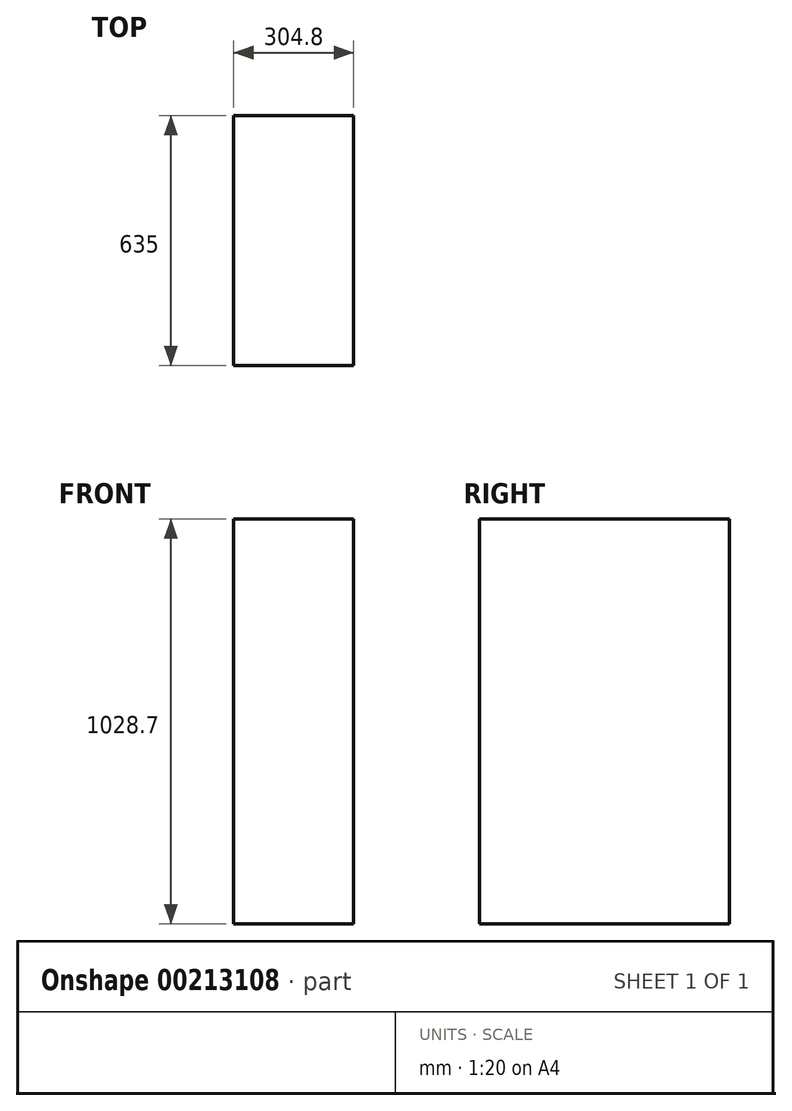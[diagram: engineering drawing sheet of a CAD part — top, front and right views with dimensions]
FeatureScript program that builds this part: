
annotation { "Feature Type Name" : "Feature", "Feature Type Description" : "" }
export const myFeature = defineFeature(function(context is Context, id is Id, definition is map)
    precondition{}
    {
        {
            var Q0;
            Q0=qCreatedBy(makeId("Front.planeOp"),FACE);
            var sketch = newSketch(context, id + "F0", { "sketchPlane" : qUnion([Q0])});
            skLineSegment(sketch, "E0.bottom", {"start": v(-149.3, 834.9) * mm, "end": v(155.5, 834.9) * mm});
            skLineSegment(sketch, "E0.top", {"start": v(-149.3, -193.8) * mm, "end": v(155.5, -193.8) * mm});
            skLineSegment(sketch, "E0.left", {"start": v(-149.3, 834.9) * mm, "end": v(-149.3, -193.8) * mm});
            skLineSegment(sketch, "E0.right", {"start": v(155.5, 834.9) * mm, "end": v(155.5, -193.8) * mm});
            skSolve(sketch);
        }
        {
            var Q0;
            Q0=makeQuery(id+"F0.imprint","IMPRINT",FACE,{"disambiguationData":[TD([[makeQuery(id+"F0.imprint","IMPRINT",EDGE,{"derivedFrom":sQuery(id+"F0.wireOp",EDGE,"E0.bottom")}),-1.0]])]});
            extrude(context, id + "F1", {"entities" : qUnion([Q0]), "depth" : 635 * mm});
        }
    });
